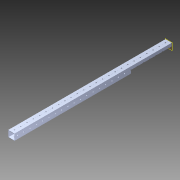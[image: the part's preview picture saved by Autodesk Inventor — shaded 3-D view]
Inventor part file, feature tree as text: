
AUTODESK INVENTOR PART (.ipt)
format: ipt  version: 2014 (Build 180170000, 170)  size: 1,342,976 bytes
history: native  units: in
note: dims shown in document units (in); Inventor stores cm internally (conversion verified against a paired STEP export)
features: extrude x3, sketch x3, reference x2, pattern_circular x1, other x1, plane x1, imported_body x1
ambient origin geometry x8: Origin, YZ Plane, XZ Plane, XY Plane, X Axis, Y Axis, Z Axis, Center Point
bodies: Body1 (feature_tree)
feature tree (12):
  pattern_circular  "CirPattern2"
  other  "217-3426-STEP1"
  plane  "Work Plane1"
  extrude  "Extrusion1"  Depth=3937.0079in TaperAngle=0.0deg
  extrude  "Extrusion3"  Depth=0.5in
  extrude  "Extrusion4"  Depth=0.0787in
  imported_body  "Base1"
  sketch  "Sketch1"  dims[d0=-25.0in d1=3937.0079in d2=0.0in]
  sketch  "Sketch4"  dims[d10=3.937in d11=0.0in d12=0.5in]
  reference  "Reference2"
  reference  "Reference3"
  sketch  "Sketch5"  dims[d13=6.5in d14=0.0787in d15=3.937in d16=0.0in]
